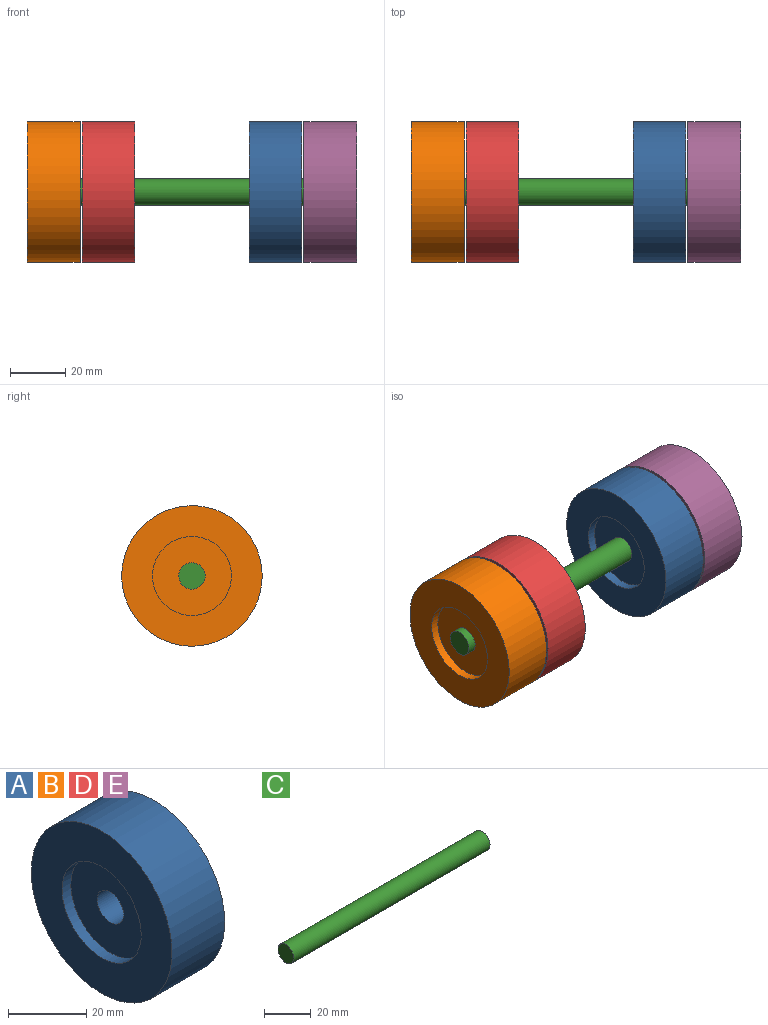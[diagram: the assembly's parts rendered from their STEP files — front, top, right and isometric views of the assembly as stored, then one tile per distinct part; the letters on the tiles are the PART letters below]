
ASSEMBLY  parts=5 mates=4
PART A: 8 faces, bbox 19.1x50.8x50.8 mm
  f0: cylinder r=4.76mm len=12.7mm, axis (1,0,0), area 380mm2, adj f1,f7
  f1: plane 28.58x28.58mm, normal (-1,0,0), area 570mm2, adj f0,f2
  f2: cylinder r=14.29mm len=28.58mm, axis (1,0,0), area 285mm2, adj f1,f3
  f3: plane 50.8x50.8mm, normal (-1,0,0), area 1385.5mm2, adj f2,f4
  f4: cylinder r=25.4mm len=50.8mm, axis (1,0,0), area 3040.2mm2, adj f3,f5
  f5: plane 50.8x50.8mm, normal (1,0,0), area 1385.5mm2, adj f4,f6
  f6: cylinder r=14.29mm len=28.58mm, axis (1,0,0), area 285mm2, adj f5,f7
  f7: plane 28.58x28.58mm, normal (1,0,0), area 570mm2, adj f0,f6
PART B: same geometry as A
PART C: 3 faces, bbox 119.1x9.5x9.5 mm
  f0: cylinder r=4.76mm len=119.06mm, axis (-1,0,0), area 3562.8mm2, adj f1,f2
  f1: plane 9.53x9.53mm, normal (1,0,0), area 71.3mm2, adj f0
  f2: plane 9.53x9.53mm, normal (-1,0,0), area 71.3mm2, adj f0
PART D: same geometry as A
PART E: same geometry as A
PLACE A rot(axis=(1,0,0),15.3deg) t=(-11.91,-38.15,-16.99)mm
PLACE B rot(axis=(1,0,0),15.3deg) t=(-92.08,-38.15,-16.99)mm
PLACE C rot(axis=(1,0,0),15.3deg) t=(0,-205.08,-62.54)mm fixed
PLACE D rot(axis=(1,0,0),15.3deg) t=(-72.23,-38.15,-16.99)mm
PLACE E rot(axis=(1,0,0),15.3deg) t=(7.94,-38.15,-16.99)mm
MATE fastened D.f0 <-> B.f0  axis (1,0,0) through (-39.69,0,0)mm
MATE fastened C.f0 <-> E.f0  axis (1,0,0) through (59.53,0,0)mm
MATE fastened A.f0 <-> E.f0  axis (1,0,0) through (39.69,0,0)mm
MATE fastened B.f0 <-> C.f0  axis (1,0,0) through (-59.53,0,0)mm
